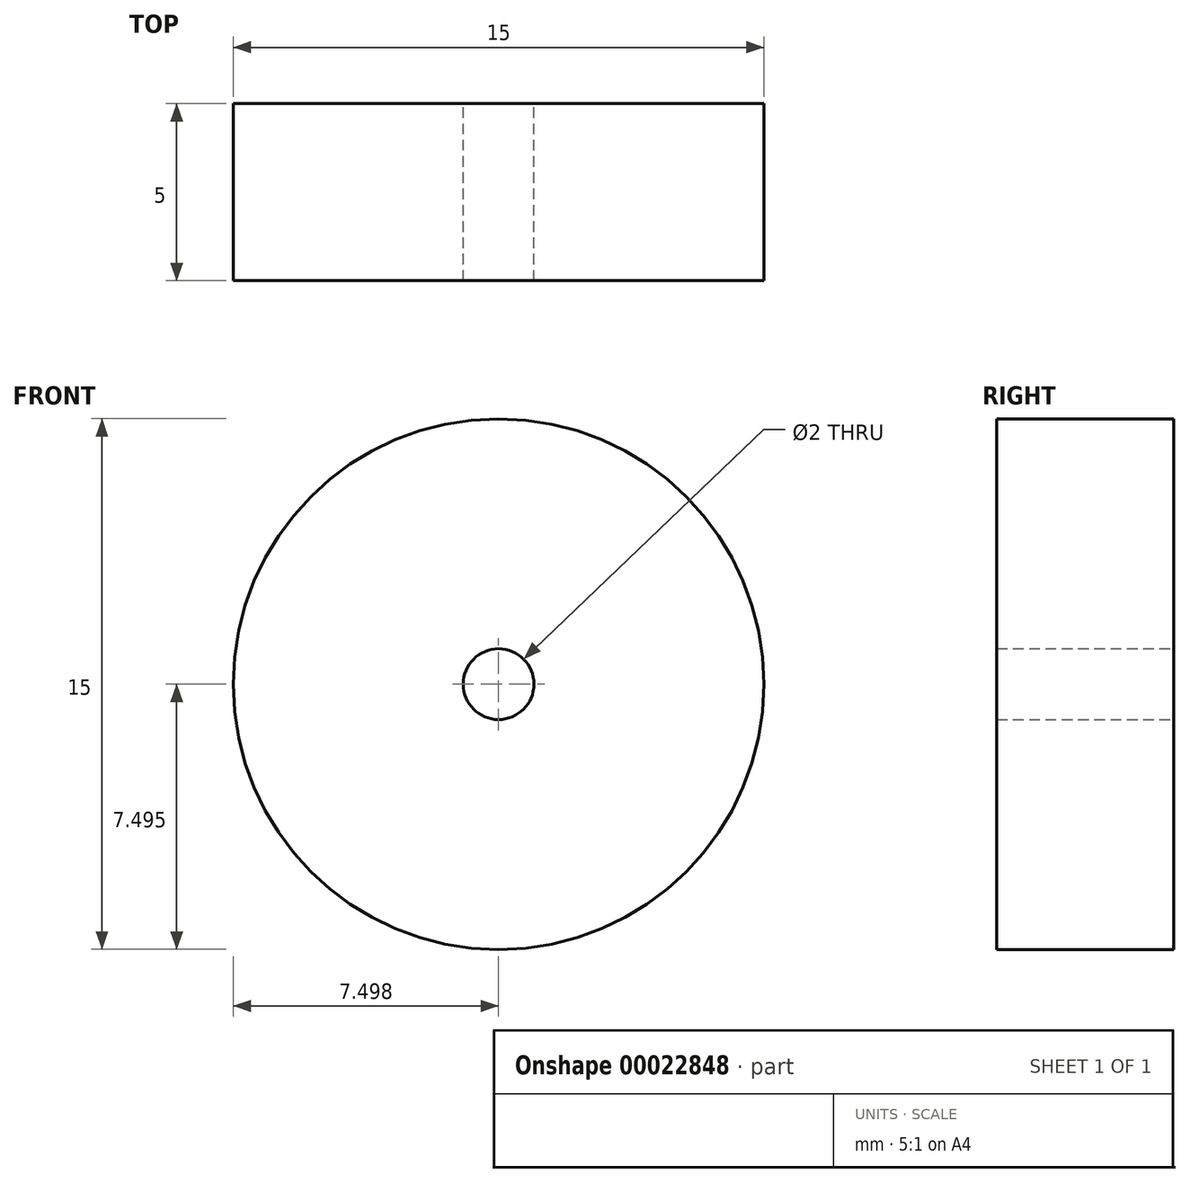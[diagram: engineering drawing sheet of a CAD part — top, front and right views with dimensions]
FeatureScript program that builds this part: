
annotation { "Feature Type Name" : "Feature", "Feature Type Description" : "" }
export const myFeature = defineFeature(function(context is Context, id is Id, definition is map)
    precondition{}
    {
        {
            var Q0;
            Q0=qCreatedBy(makeId("Front.planeOp"),FACE);
            var sketch = newSketch(context, id + "F0", { "sketchPlane" : qUnion([Q0])});
            skCircle(sketch, "E0", {"center": v(-34.04, 11.93) * mm, "radius": 7.5 * mm});
            skCircle(sketch, "E1", {"center": v(-34.04, 11.93) * mm, "radius": 1 * mm});
            skSolve(sketch);
        }
        {
            var Q0;
            Q0=qSketchRegion(id+"F0",true);
            extrude(context, id + "F1", {"entities" : qUnion([Q0]), "endBound" : BoundingType.SYMMETRIC, "depth" : 5 * mm});
        }
    });
